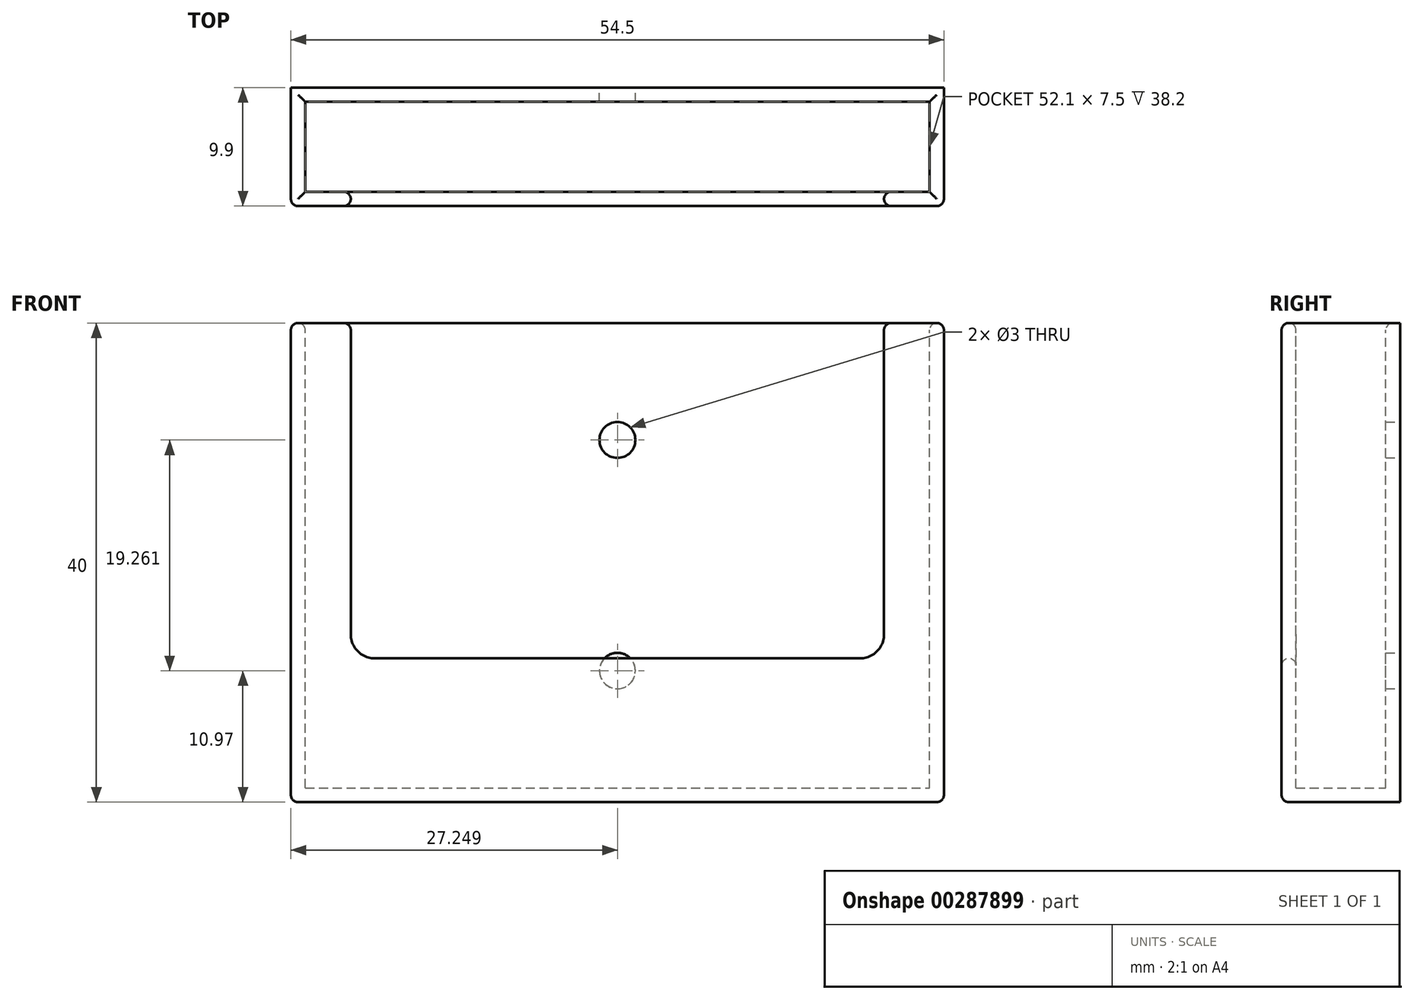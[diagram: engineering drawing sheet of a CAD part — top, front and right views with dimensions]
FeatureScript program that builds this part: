
annotation { "Feature Type Name" : "Feature", "Feature Type Description" : "" }
export const myFeature = defineFeature(function(context is Context, id is Id, definition is map)
    precondition{}
    {
        {
            var Q0;
            Q0=qCreatedBy(makeId("Front.planeOp"),FACE);
            var sketch = newSketch(context, id + "F0", { "sketchPlane" : qUnion([Q0])});
            skLineSegment(sketch, "E0.bottom", {"start": v(-30.18, 0) * mm, "end": v(24.32, 0) * mm});
            skLineSegment(sketch, "E0.top", {"start": v(-30.18, -40) * mm, "end": v(24.32, -40) * mm});
            skLineSegment(sketch, "E0.left", {"start": v(-30.18, 0) * mm, "end": v(-30.18, -40) * mm});
            skLineSegment(sketch, "E0.right", {"start": v(24.32, 0) * mm, "end": v(24.32, -40) * mm});
            skLineSegment(sketch, "E1.bottom", {"start": v(-28.98, 0) * mm, "end": v(23.12, 0) * mm});
            skLineSegment(sketch, "E1.top", {"start": v(-28.98, -38.8) * mm, "end": v(23.12, -38.8) * mm});
            skLineSegment(sketch, "E1.left", {"start": v(-28.98, 0) * mm, "end": v(-28.98, -38.8) * mm});
            skLineSegment(sketch, "E1.right", {"start": v(23.12, 0) * mm, "end": v(23.12, -38.8) * mm});
            skLineSegment(sketch, "E2", {"start": v(-28.98, -38.8) * mm, "end": v(23.12, 0) * mm});
            skLineSegment(sketch, "E3", {"start": v(-28.98, 0) * mm, "end": v(23.12, -38.8) * mm});
            skLineSegment(sketch, "E4.bottom", {"start": v(-2.93, -19.4) * mm, "end": v(3.3, -19.4) * mm});
            skLineSegment(sketch, "E4.top", {"start": v(-2.93, -29.03) * mm, "end": v(3.3, -29.03) * mm});
            skLineSegment(sketch, "E4.left", {"start": v(-2.93, -19.4) * mm, "end": v(-2.93, -29.03) * mm});
            skLineSegment(sketch, "E4.right", {"start": v(3.3, -19.4) * mm, "end": v(3.3, -29.03) * mm});
            skLineSegment(sketch, "E5.bottom", {"start": v(-2.93, -19.4) * mm, "end": v(3.42, -19.4) * mm});
            skLineSegment(sketch, "E5.top", {"start": v(-2.93, -9.77) * mm, "end": v(3.42, -9.77) * mm});
            skLineSegment(sketch, "E5.left", {"start": v(-2.93, -19.4) * mm, "end": v(-2.93, -9.77) * mm});
            skLineSegment(sketch, "E5.right", {"start": v(3.42, -19.4) * mm, "end": v(3.42, -9.77) * mm});
            skCircle(sketch, "E6", {"center": v(-2.93, -9.77) * mm, "radius": 1.5 * mm});
            skCircle(sketch, "E7", {"center": v(-2.93, -29.03) * mm, "radius": 1.5 * mm});
            skSolve(sketch);
        }
        {
            var Q0;
            Q0 = qSketchRegion(id + "F0", true);
            var Q1;
            {var subQ1=sQuery(id+"F0.wireOp",EDGE,"E1.top");Q1=makeQuery(id+"F0.imprint","IMPRINT",FACE,{"disambiguationData":[TD([[makeQuery(id+"F0.imprint","IMPRINT",EDGE,{"derivedFrom":subQ1}),1.0]])]});}
            var Q2;
            {var subQ0=sQuery(id+"F0.wireOp",EDGE,"E4.right");var subQ1=sQuery(id+"F0.wireOp",EDGE,"E4.top");var subQ2=makeQuery(id+"F0.imprint","INTERSECT",VERTEX,{"derivedFrom":[subQ1,subQ0]});Q2=makeQuery(id+"F0.imprint","IMPRINT",FACE,{"disambiguationData":[TD([[makeQuery(id+"F0.imprint","IMPRINT",EDGE,{"disambiguationData":[TD([[subQ2,1.0]])],"derivedFrom":subQ1}),1.0]])]});}
            var Q3;
            {var subQ0=sQuery(id+"F0.wireOp",EDGE,"E5.bottom");var subQ3=sQuery(id+"F0.wireOp",EDGE,"E4.right");var subQ5=makeQuery(id+"F0.imprint","INTERSECT",VERTEX,{"derivedFrom":[subQ3,subQ0]});Q3=makeQuery(id+"F0.imprint","IMPRINT",FACE,{"disambiguationData":[TD([[makeQuery(id+"F0.imprint","IMPRINT",EDGE,{"disambiguationData":[TD([[subQ5,-1.0]])],"derivedFrom":subQ3}),-1.0]])]});}
            var Q4;
            {var subQ0=sQuery(id+"F0.wireOp",EDGE,"E5.bottom");var subQ5=makeQuery(id+"F0.imprint","INTERSECT",VERTEX,{"derivedFrom":[sQuery(id+"F0.wireOp",EDGE,"E4.right"),subQ0]});Q4=makeQuery(id+"F0.imprint","IMPRINT",FACE,{"disambiguationData":[TD([[makeQuery(id+"F0.imprint","IMPRINT",EDGE,{"disambiguationData":[TD([[subQ5,-1.0]])],"derivedFrom":subQ0}),1.0]])]});}
            var Q5;
            {var subQ0=sQuery(id+"F0.wireOp",EDGE,"E5.right");var subQ1=sQuery(id+"F0.wireOp",EDGE,"E5.top");var subQ2=makeQuery(id+"F0.imprint","INTERSECT",VERTEX,{"derivedFrom":[subQ1,subQ0]});Q5=makeQuery(id+"F0.imprint","IMPRINT",FACE,{"disambiguationData":[TD([[makeQuery(id+"F0.imprint","IMPRINT",EDGE,{"disambiguationData":[TD([[subQ2,1.0]])],"derivedFrom":subQ1}),-1.0]])]});}
            extrude(context, id + "F1", {"entities" : qUnion([Q0, Q1, Q2, Q3, Q4, Q5]), "depth" : 1.2 * mm});
        }
        {
            var Q0;
            Q0=makeQuery(id+"F1.opExtrude","CAP_FACE",FACE,{"disambiguationData":[OSD([sQuery(id+"F0.wireOp",EDGE,"E0.bottom"),sQuery(id+"F0.wireOp",EDGE,"E0.top"),sQuery(id+"F0.wireOp",EDGE,"E0.left"),sQuery(id+"F0.wireOp",EDGE,"E0.right"),sQuery(id+"F0.wireOp",EDGE,"E1.bottom"),sQuery(id+"F0.wireOp",EDGE,"E6"),sQuery(id+"F0.wireOp",EDGE,"E7")])],"isStart":false});
            var sketch = newSketch(context, id + "F2", { "sketchPlane" : qUnion([Q0])});
            skLineSegment(sketch, "E8.bottom", {"start": v(-30.18, -40) * mm, "end": v(24.32, -40) * mm});
            skLineSegment(sketch, "E8.top", {"start": v(-30.18, 0) * mm, "end": v(24.32, 0) * mm});
            skLineSegment(sketch, "E8.left", {"start": v(-30.18, -40) * mm, "end": v(-30.18, 0) * mm});
            skLineSegment(sketch, "E8.right", {"start": v(24.32, -40) * mm, "end": v(24.32, 0) * mm});
            skLineSegment(sketch, "E9.0", {"start": v(-28.98, -38.8) * mm, "end": v(-28.98, 0) * mm});
            skLineSegment(sketch, "E9.1", {"start": v(-28.98, -38.8) * mm, "end": v(23.12, -38.8) * mm});
            skLineSegment(sketch, "E9.2", {"start": v(23.12, -38.8) * mm, "end": v(23.12, 0) * mm});
            skSolve(sketch);
        }
        {
            var Q0;
            Q0=makeQuery(id+"F2.imprint","IMPRINT",FACE,{"disambiguationData":[TD([[makeQuery(id+"F2.imprint","IMPRINT",EDGE,{"derivedFrom":sQuery(id+"F2.wireOp",EDGE,"E8.bottom")}),1.0]])]});
            extrude(context, id + "F3", {"entities" : qUnion([Q0]), "operationType" : NewBodyOperationType.ADD, "depth" : 7.5 * mm});
        }
        {
            var Q0;
            Q0=makeQuery(id+"F3.opExtrude","CAP_FACE",FACE,{"disambiguationData":[OSD([sQuery(id+"F2.wireOp",EDGE,"E8.bottom"),sQuery(id+"F2.wireOp",EDGE,"E8.top"),sQuery(id+"F2.wireOp",EDGE,"E8.left"),sQuery(id+"F2.wireOp",EDGE,"E8.right"),sQuery(id+"F2.wireOp",EDGE,"E9.0"),sQuery(id+"F2.wireOp",EDGE,"E9.1"),sQuery(id+"F2.wireOp",EDGE,"E9.2")])],"isStart":false});
            var sketch = newSketch(context, id + "F4", { "sketchPlane" : qUnion([Q0])});
            skLineSegment(sketch, "E10.bottom", {"start": v(-30.18, -40) * mm, "end": v(24.32, -40) * mm});
            skLineSegment(sketch, "E10.top", {"start": v(-30.18, 0) * mm, "end": v(24.32, 0) * mm});
            skLineSegment(sketch, "E10.left", {"start": v(-30.18, -40) * mm, "end": v(-30.18, 0) * mm});
            skLineSegment(sketch, "E10.right", {"start": v(24.32, -40) * mm, "end": v(24.32, 0) * mm});
            skLineSegment(sketch, "E11.0", {"start": v(-25.18, -26) * mm, "end": v(-25.18, 0) * mm});
            skLineSegment(sketch, "E12.0", {"start": v(19.32, -26) * mm, "end": v(19.32, 0) * mm});
            skLineSegment(sketch, "E13.0", {"start": v(-23.18, -28) * mm, "end": v(17.32, -28) * mm});
            skArc(sketch, "E14.filletArc", {"start": v(-25.18, -26) * mm, "mid": v(-24.6, -27.41) * mm, "end": v(-23.18, -28) * mm});
            skArc(sketch, "E15.filletArc", {"start": v(17.32, -28) * mm, "mid": v(18.73, -27.41) * mm, "end": v(19.32, -26) * mm});
            skSolve(sketch);
        }
        {
            var Q0;
            {var subQ0=sQuery(id+"F4.wireOp",EDGE,"E11.0");Q0=makeQuery(id+"F4.imprint","IMPRINT",FACE,{"disambiguationData":[TD([[makeQuery(id+"F4.imprint","IMPRINT",EDGE,{"derivedFrom":subQ0}),1.0]])]});}
            var Q1;
            Q1=makeQuery(id+"F4.imprint","IMPRINT",FACE,{"disambiguationData":[TD([[makeQuery(id+"F4.imprint","IMPRINT",EDGE,{"derivedFrom":sQuery(id+"F4.wireOp",EDGE,"E10.bottom")}),1.0]])]});
            extrude(context, id + "F5", {"entities" : qUnion([Q0, Q1]), "operationType" : NewBodyOperationType.ADD, "depth" : 1.2 * mm});
        }
        {
            var Q0;
            Q0=makeQuery(id+"F5.boolean.opBoolean","MERGE",EDGE,{"derivedFrom":[makeQuery(id+"F3.boolean.opBoolean","MERGE",EDGE,{"derivedFrom":[makeQuery(id+"F1.opExtrude","SWEPT_EDGE",EDGE,{"disambiguationData":[OSD([sQuery(id+"F0.wireOp",EDGE,"E0.top"),sQuery(id+"F0.wireOp",EDGE,"E0.left")])]}),makeQuery(id+"F3.opExtrude","SWEPT_EDGE",EDGE,{"disambiguationData":[OSD([sQuery(id+"F2.wireOp",EDGE,"E8.bottom"),sQuery(id+"F2.wireOp",EDGE,"E8.left")])]})]}),makeQuery(id+"F5.opExtrude","SWEPT_EDGE",EDGE,{"disambiguationData":[OSD([sQuery(id+"F4.wireOp",EDGE,"E10.bottom"),sQuery(id+"F4.wireOp",EDGE,"E10.left")])]})]});
            var Q1;
            Q1=makeQuery(id+"F5.boolean.opBoolean","MERGE",EDGE,{"derivedFrom":[makeQuery(id+"F3.boolean.opBoolean","MERGE",EDGE,{"derivedFrom":[makeQuery(id+"F1.opExtrude","SWEPT_EDGE",EDGE,{"disambiguationData":[OSD([sQuery(id+"F0.wireOp",EDGE,"E0.top"),sQuery(id+"F0.wireOp",EDGE,"E0.right")])]}),makeQuery(id+"F3.opExtrude","SWEPT_EDGE",EDGE,{"disambiguationData":[OSD([sQuery(id+"F2.wireOp",EDGE,"E8.bottom"),sQuery(id+"F2.wireOp",EDGE,"E8.right")])]})]}),makeQuery(id+"F5.opExtrude","SWEPT_EDGE",EDGE,{"disambiguationData":[OSD([sQuery(id+"F4.wireOp",EDGE,"E10.bottom"),sQuery(id+"F4.wireOp",EDGE,"E10.right")])]})]});
            var Q2;
            Q2=makeQuery(id+"F5.boolean.opBoolean","MERGE",EDGE,{"derivedFrom":[makeQuery(id+"F3.boolean.opBoolean","MERGE",EDGE,{"derivedFrom":[makeQuery(id+"F1.opExtrude","SWEPT_EDGE",EDGE,{"disambiguationData":[OSD([sQuery(id+"F0.wireOp",EDGE,"E0.bottom"),sQuery(id+"F0.wireOp",EDGE,"E0.left")])]}),makeQuery(id+"F3.opExtrude","SWEPT_EDGE",EDGE,{"disambiguationData":[OSD([sQuery(id+"F2.wireOp",EDGE,"E8.top"),sQuery(id+"F2.wireOp",EDGE,"E8.left")])]})]}),makeQuery(id+"F5.opExtrude","SWEPT_EDGE",EDGE,{"disambiguationData":[OSD([sQuery(id+"F4.wireOp",EDGE,"E10.top"),sQuery(id+"F4.wireOp",EDGE,"E10.left")])]})]});
            var Q3;
            {var subQ0=sQuery(id+"F4.wireOp",EDGE,"E10.top");var subQ1=makeQuery(id+"F4.imprint","INTERSECT",VERTEX,{"derivedFrom":[makeQuery(id+"F3.opExtrude","CAP_EDGE",EDGE,{"disambiguationData":[OSD([sQuery(id+"F2.wireOp",EDGE,"E9.0")])],"isStart":false}),subQ0]});Q3=makeQuery(id+"F5.opExtrude","CAP_EDGE",EDGE,{"disambiguationData":[OSD([subQ0]),TDD([makeQuery(id+"F4.imprint","IMPRINT",EDGE,{"disambiguationData":[TD([[makeQuery(id+"F4.imprint","INTERSECT",VERTEX,{"derivedFrom":[subQ0,sQuery(id+"F4.wireOp",EDGE,"E10.left")]}),-1.0]])],"derivedFrom":subQ0}),makeQuery(id+"F4.imprint","IMPRINT",EDGE,{"disambiguationData":[TD([[subQ1,-1.0]])],"derivedFrom":subQ0})])],"isStart":false});}
            var Q4;
            Q4=makeQuery(id+"F5.boolean.opBoolean","MERGE",EDGE,{"derivedFrom":[makeQuery(id+"F3.boolean.opBoolean","MERGE",EDGE,{"derivedFrom":[makeQuery(id+"F1.opExtrude","SWEPT_EDGE",EDGE,{"disambiguationData":[OSD([sQuery(id+"F0.wireOp",EDGE,"E0.bottom"),sQuery(id+"F0.wireOp",EDGE,"E0.right")])]}),makeQuery(id+"F3.opExtrude","SWEPT_EDGE",EDGE,{"disambiguationData":[OSD([sQuery(id+"F2.wireOp",EDGE,"E8.top"),sQuery(id+"F2.wireOp",EDGE,"E8.right")])]})]}),makeQuery(id+"F5.opExtrude","SWEPT_EDGE",EDGE,{"disambiguationData":[OSD([sQuery(id+"F4.wireOp",EDGE,"E10.top"),sQuery(id+"F4.wireOp",EDGE,"E10.right")])]})]});
            var Q5;
            {var subQ0=sQuery(id+"F4.wireOp",EDGE,"E10.top");var subQ1=makeQuery(id+"F4.imprint","INTERSECT",VERTEX,{"derivedFrom":[makeQuery(id+"F3.opExtrude","CAP_EDGE",EDGE,{"disambiguationData":[OSD([sQuery(id+"F2.wireOp",EDGE,"E9.2")])],"isStart":false}),subQ0]});Q5=makeQuery(id+"F5.opExtrude","CAP_EDGE",EDGE,{"disambiguationData":[OSD([subQ0]),TDD([makeQuery(id+"F4.imprint","IMPRINT",EDGE,{"disambiguationData":[TD([[subQ1,1.0]])],"derivedFrom":subQ0}),makeQuery(id+"F4.imprint","IMPRINT",EDGE,{"disambiguationData":[TD([[makeQuery(id+"F4.imprint","INTERSECT",VERTEX,{"derivedFrom":[subQ0,sQuery(id+"F4.wireOp",EDGE,"E10.right")]}),1.0]])],"derivedFrom":subQ0})])],"isStart":false});}
            var Q6;
            Q6=makeQuery(id+"F5.opExtrude","CAP_EDGE",EDGE,{"disambiguationData":[OSD([sQuery(id+"F4.wireOp",EDGE,"E10.bottom")])],"isStart":false});
            var Q7;
            Q7=makeQuery(id+"F5.opExtrude","CAP_EDGE",EDGE,{"disambiguationData":[OSD([sQuery(id+"F4.wireOp",EDGE,"E10.right")])],"isStart":false});
            var Q8;
            Q8=makeQuery(id+"F5.opExtrude","CAP_EDGE",EDGE,{"disambiguationData":[OSD([sQuery(id+"F4.wireOp",EDGE,"E10.left")])],"isStart":false});
            var Q9;
            Q9=makeQuery(id+"F5.opExtrude","CAP_EDGE",EDGE,{"disambiguationData":[OSD([sQuery(id+"F4.wireOp",EDGE,"E11.0")])],"isStart":false});
            var Q10;
            Q10=makeQuery(id+"F5.opExtrude","CAP_EDGE",EDGE,{"disambiguationData":[OSD([sQuery(id+"F4.wireOp",EDGE,"E13.0")])],"isStart":true});
            var Q11;
            Q11=makeQuery(id+"F5.opExtrude","CAP_EDGE",EDGE,{"disambiguationData":[OSD([sQuery(id+"F4.wireOp",EDGE,"E12.0")])],"isStart":true});
            var Q12;
            {var subQ0=sQuery(id+"F4.wireOp",EDGE,"E10.top");var subQ1=makeQuery(id+"F4.imprint","INTERSECT",VERTEX,{"derivedFrom":[makeQuery(id+"F3.opExtrude","CAP_EDGE",EDGE,{"disambiguationData":[OSD([sQuery(id+"F2.wireOp",EDGE,"E9.0")])],"isStart":false}),subQ0]});Q12=makeQuery(id+"F5.opExtrude","CAP_EDGE",EDGE,{"disambiguationData":[OSD([subQ0]),TDD([makeQuery(id+"F4.imprint","IMPRINT",EDGE,{"disambiguationData":[TD([[makeQuery(id+"F4.imprint","INTERSECT",VERTEX,{"derivedFrom":[subQ0,sQuery(id+"F4.wireOp",EDGE,"E10.left")]}),-1.0]])],"derivedFrom":subQ0}),makeQuery(id+"F4.imprint","IMPRINT",EDGE,{"disambiguationData":[TD([[subQ1,-1.0]])],"derivedFrom":subQ0})])],"isStart":true});}
            var Q13;
            Q13=makeQuery(id+"F3.opExtrude","SWEPT_EDGE",EDGE,{"disambiguationData":[OSD([sQuery(id+"F2.wireOp",EDGE,"E8.top"),sQuery(id+"F2.wireOp",EDGE,"E9.0")])]});
            var Q14;
            Q14=makeQuery(id+"F3.opExtrude","SWEPT_EDGE",EDGE,{"disambiguationData":[OSD([sQuery(id+"F2.wireOp",EDGE,"E8.top"),sQuery(id+"F2.wireOp",EDGE,"E9.2")])]});
            var Q15;
            {var subQ0=sQuery(id+"F4.wireOp",EDGE,"E10.top");var subQ1=makeQuery(id+"F4.imprint","INTERSECT",VERTEX,{"derivedFrom":[makeQuery(id+"F3.opExtrude","CAP_EDGE",EDGE,{"disambiguationData":[OSD([sQuery(id+"F2.wireOp",EDGE,"E9.2")])],"isStart":false}),subQ0]});Q15=makeQuery(id+"F5.opExtrude","CAP_EDGE",EDGE,{"disambiguationData":[OSD([subQ0]),TDD([makeQuery(id+"F4.imprint","IMPRINT",EDGE,{"disambiguationData":[TD([[subQ1,1.0]])],"derivedFrom":subQ0}),makeQuery(id+"F4.imprint","IMPRINT",EDGE,{"disambiguationData":[TD([[makeQuery(id+"F4.imprint","INTERSECT",VERTEX,{"derivedFrom":[subQ0,sQuery(id+"F4.wireOp",EDGE,"E10.right")]}),1.0]])],"derivedFrom":subQ0})])],"isStart":true});}
            var Q16;
            Q16=makeQuery(id+"F5.opExtrude","SWEPT_EDGE",EDGE,{"disambiguationData":[OSD([sQuery(id+"F4.wireOp",EDGE,"E10.top"),sQuery(id+"F4.wireOp",EDGE,"E12.0")])]});
            var Q17;
            Q17=makeQuery(id+"F5.opExtrude","SWEPT_EDGE",EDGE,{"disambiguationData":[OSD([sQuery(id+"F4.wireOp",EDGE,"E10.top"),sQuery(id+"F4.wireOp",EDGE,"E11.0")])]});
            var Q18;
            Q18=makeQuery(id+"F1.opExtrude","CAP_EDGE",EDGE,{"disambiguationData":[OSD([sQuery(id+"F0.wireOp",EDGE,"E0.bottom"),sQuery(id+"F0.wireOp",EDGE,"E1.bottom")])],"isStart":false});
            fillet(context, id + "F6", {"entities" : qUnion([Q0, Q1, Q2, Q3, Q4, Q5, Q6, Q7, Q8, Q9, Q10, Q11, Q12, Q13, Q14, Q15, Q16, Q17, Q18]), "radius" : 0.6 * mm, "tangentPropagation" : true, "allowEdgeOverflow" : false});
        }
    });
